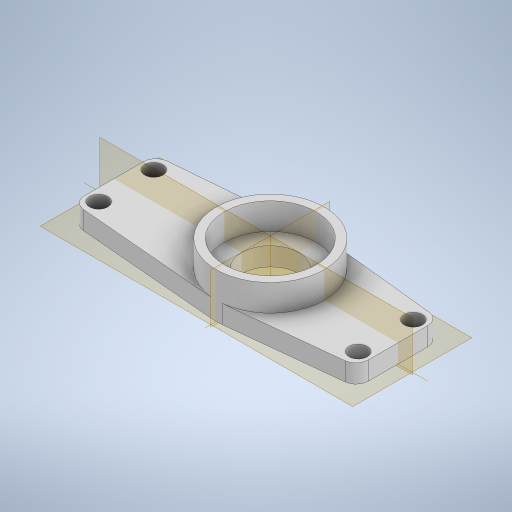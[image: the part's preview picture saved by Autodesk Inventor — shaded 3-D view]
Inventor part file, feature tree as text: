
AUTODESK INVENTOR PART (.ipt)
format: ipt  version: 2023 (Build 270158000, 158)  size: 314,880 bytes
history: native  units: in
note: dims shown in document units (in); Inventor stores cm internally (conversion verified against a paired STEP export)
features: extrude x2, fillet x2, sketch x2
ambient origin geometry x8: Origin, YZ Plane, XZ Plane, XY Plane, X Axis, Y Axis, Z Axis, Center Point
bodies: Solid1 (feature_tree)
feature tree (6):
  extrude  "Extrusion1"  Depth=1.2303in
  extrude  "Extrusion2"  Depth=0.3937in
  fillet  "Fillet1"  Radius=1.5059in
  fillet  "Fillet2"  Radius=0.3937in
  sketch  "Sketch1"  dims[d2=0.5512in d3=1.2303in]
  sketch  "Sketch2"  dims[d4=0.3937in d5=0.3937in d6=1.5059in d7=0.3937in d8=0.3937in d9=0.1181in d10=0.2657in d11=0.2657in d12=0.1772in d13=0.1772in d14=0.1181in d15=0.2657in d16=0.2657in d17=0.1772in d18=0.1772in d19=0.1772in d20=0.0in d21=1.0433in d22=0.8858in d23=0.4331in d24=0.0in d25=0.1181in d26=0.1181in]
